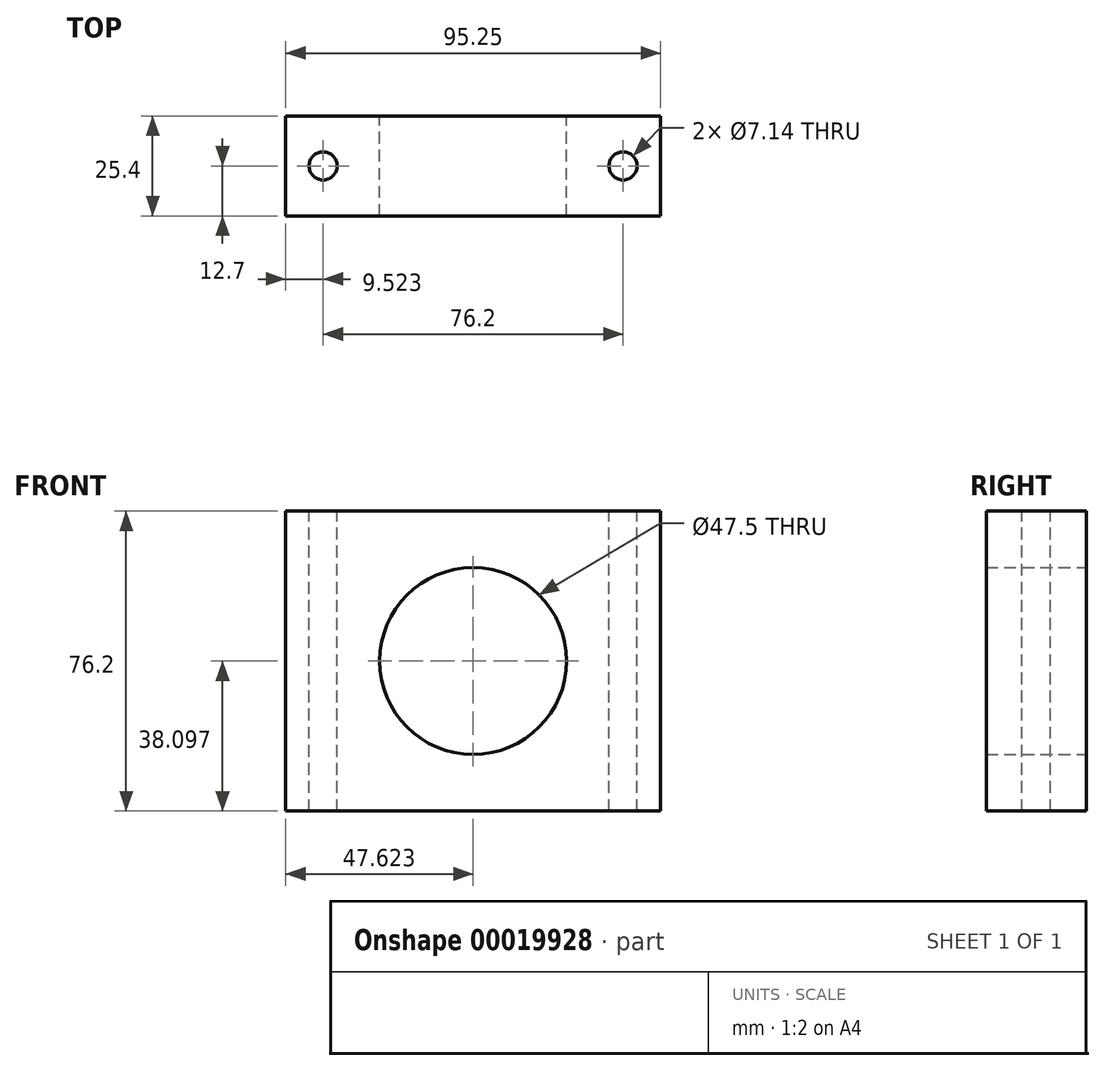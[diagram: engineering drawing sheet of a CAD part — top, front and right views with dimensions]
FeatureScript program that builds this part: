
annotation { "Feature Type Name" : "Feature", "Feature Type Description" : "" }
export const myFeature = defineFeature(function(context is Context, id is Id, definition is map)
    precondition{}
    {
        {
            var Q0;
            Q0=qCreatedBy(makeId("Front.planeOp"),FACE);
            var sketch = newSketch(context, id + "F0", { "sketchPlane" : qUnion([Q0])});
            skLineSegment(sketch, "E0.bottom", {"start": v(-34.53, 26.65) * mm, "end": v(60.72, 26.65) * mm});
            skLineSegment(sketch, "E0.top", {"start": v(-34.53, -49.55) * mm, "end": v(60.72, -49.55) * mm});
            skLineSegment(sketch, "E0.left", {"start": v(-34.53, 26.65) * mm, "end": v(-34.53, -49.55) * mm});
            skLineSegment(sketch, "E0.right", {"start": v(60.72, 26.65) * mm, "end": v(60.72, -49.55) * mm});
            skLineSegment(sketch, "E1", {"start": v(13.1, -49.55) * mm, "end": v(13.1, 26.65) * mm});
            skCircle(sketch, "E2", {"center": v(13.1, -11.45) * mm, "radius": 23.75 * mm});
            skSolve(sketch);
        }
        {
            var Q0;
            Q0 = qSketchRegion(id + "F0", true);
            extrude(context, id + "F1", {"entities" : qUnion([Q0]), "depth" : 25.4 * mm});
        }
        {
            var Q0;
            Q0=makeQuery(id+"F1.opExtrude","SWEPT_FACE",FACE,{"disambiguationData":[OSD([sQuery(id+"F0.wireOp",EDGE,"E0.bottom")])]});
            var sketch = newSketch(context, id + "F2", { "sketchPlane" : qUnion([Q0])});
            skCircle(sketch, "E3", {"center": v(-25, -12.7) * mm, "radius": 3.57 * mm});
            skCircle(sketch, "E4", {"center": v(51.2, -12.7) * mm, "radius": 3.57 * mm});
            skSolve(sketch);
        }
        {
            var Q0;
            Q0=makeQuery(id+"F2.imprint","IMPRINT",FACE,{"disambiguationData":[TD([[makeQuery(id+"F2.imprint","IMPRINT",EDGE,{"derivedFrom":sQuery(id+"F2.wireOp",EDGE,"E3")}),1.0]])]});
            var Q1;
            Q1=makeQuery(id+"F2.imprint","IMPRINT",FACE,{"disambiguationData":[TD([[makeQuery(id+"F2.imprint","IMPRINT",EDGE,{"derivedFrom":sQuery(id+"F2.wireOp",EDGE,"E4")}),1.0]])]});
            var Q2;
            Q2=sQuery(id+"F2.wireOp",EDGE,"E4");
            var Q3;
            Q3=sQuery(id+"F2.wireOp",EDGE,"E3");
            extrude(context, id + "F3", {"entities" : qUnion([Q0, Q1]), "operationType" : NewBodyOperationType.REMOVE, "surfaceEntities" : qUnion([Q2, Q3]), "endBound" : BoundingType.THROUGH_ALL, "oppositeDirection" : true, "depth" : 25.4 * mm});
        }
    });
